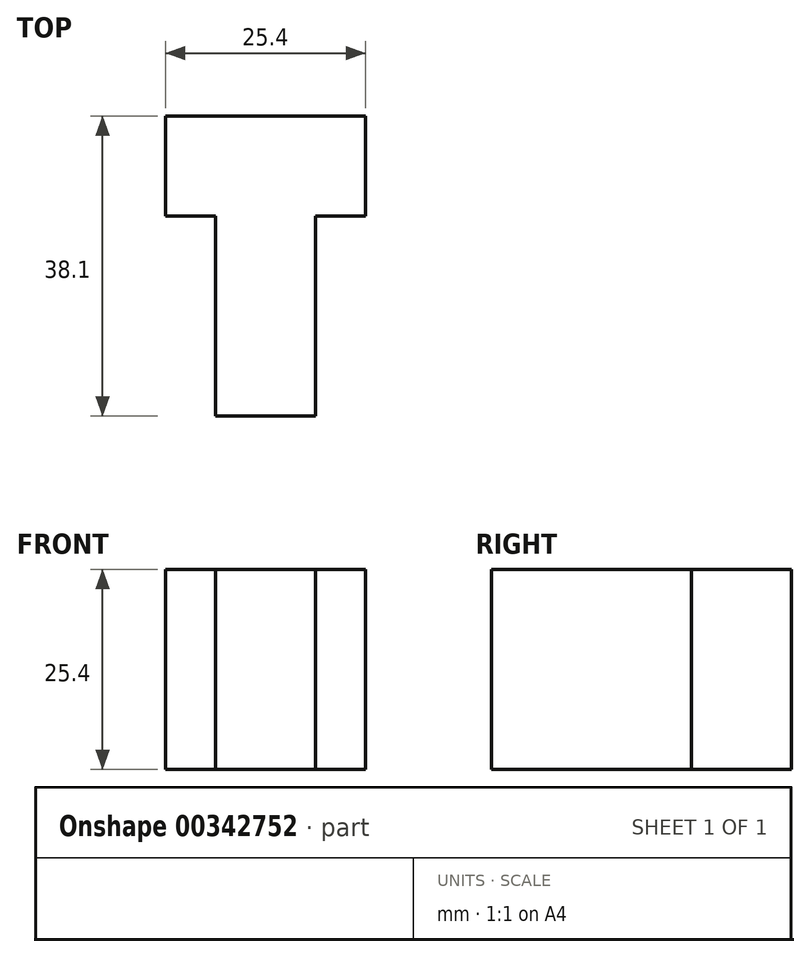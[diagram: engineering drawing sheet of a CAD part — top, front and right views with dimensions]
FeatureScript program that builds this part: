
annotation { "Feature Type Name" : "Feature", "Feature Type Description" : "" }
export const myFeature = defineFeature(function(context is Context, id is Id, definition is map)
    precondition{}
    {
        {
            var Q0;
            Q0=qCreatedBy(makeId("Top.planeOp"),FACE);
            var sketch = newSketch(context, id + "F0", { "sketchPlane" : qUnion([Q0])});
            skLineSegment(sketch, "E0", {"start": v(0, 0) * mm, "end": v(0, 25.4) * mm});
            skLineSegment(sketch, "E1", {"start": v(0, 25.4) * mm, "end": v(-6.35, 25.4) * mm});
            skLineSegment(sketch, "E2", {"start": v(-6.35, 25.4) * mm, "end": v(-6.35, 38.1) * mm});
            skLineSegment(sketch, "E3", {"start": v(-6.35, 38.1) * mm, "end": v(19.05, 38.1) * mm});
            skLineSegment(sketch, "E4", {"start": v(19.05, 38.1) * mm, "end": v(19.05, 25.4) * mm});
            skLineSegment(sketch, "E5", {"start": v(19.05, 25.4) * mm, "end": v(12.7, 25.4) * mm});
            skLineSegment(sketch, "E6", {"start": v(12.7, 25.4) * mm, "end": v(12.7, 0) * mm});
            skLineSegment(sketch, "E7", {"start": v(12.7, 0) * mm, "end": v(0, 0) * mm});
            skSolve(sketch);
        }
        {
            var Q0;
            Q0 = qSketchRegion(id + "F0", true);
            extrude(context, id + "F1", {"entities" : qUnion([Q0]), "depth" : 25.4 * mm});
        }
    });
